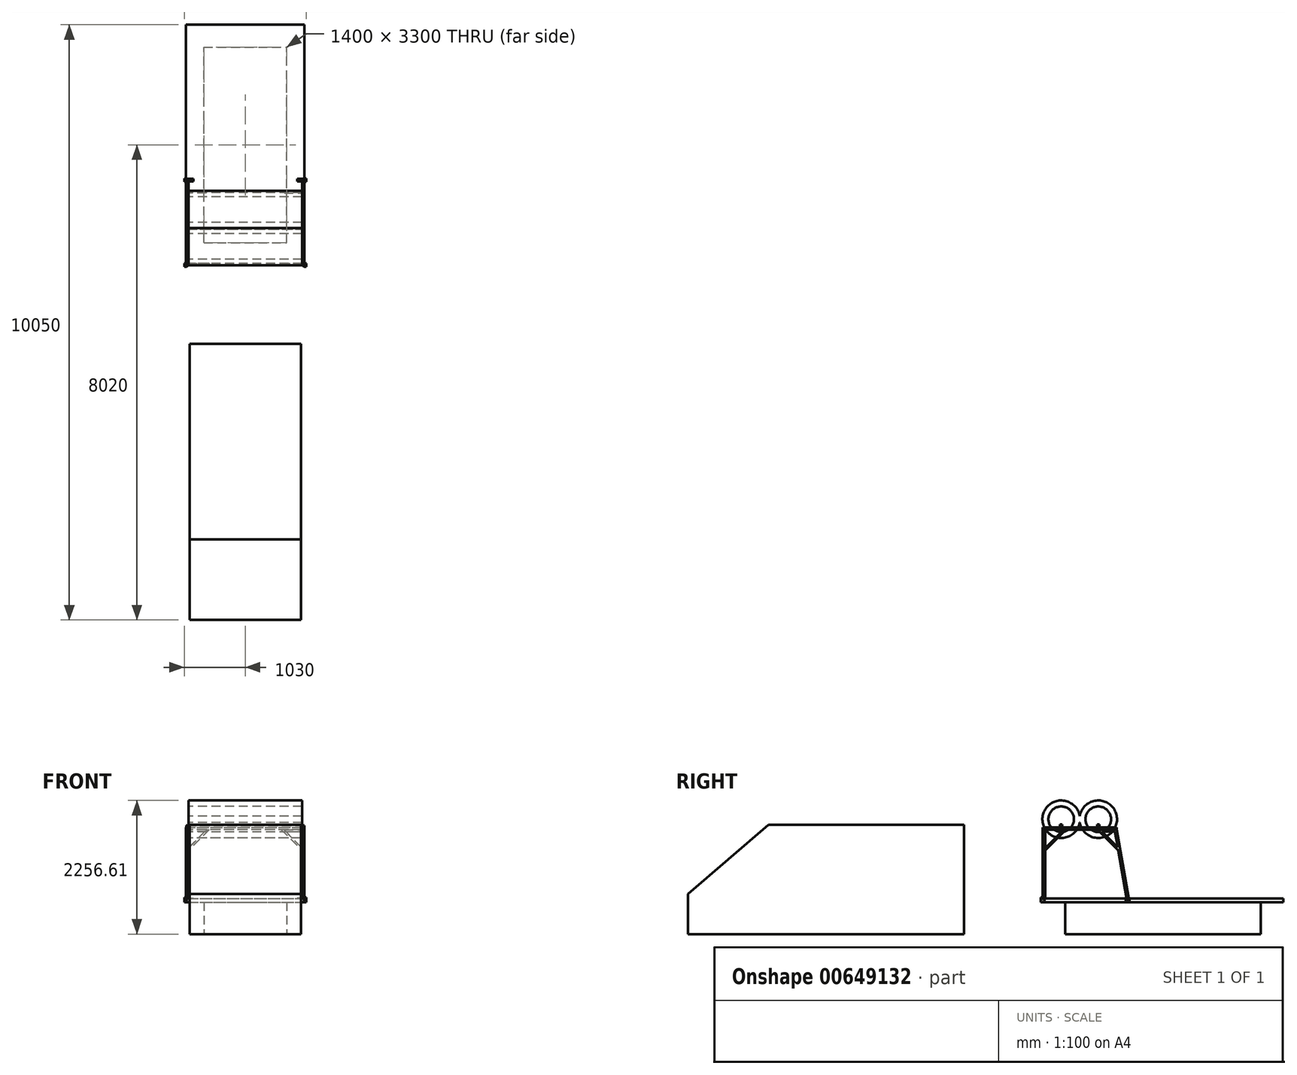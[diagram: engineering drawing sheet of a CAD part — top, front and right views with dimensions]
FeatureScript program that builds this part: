
annotation { "Feature Type Name" : "Feature", "Feature Type Description" : "" }
export const myFeature = defineFeature(function(context is Context, id is Id, definition is map)
    precondition{}
    {
        {
            var Q0;
            Q0=qCreatedBy(makeId("Top.planeOp"),FACE);
            cPlane(context, id + "F0", {"entities" : qUnion([Q0]), "cplaneType" : CPlaneType.OFFSET, "offset" : 600 * mm, "width" : 150 * mm, "height" : 150 * mm});
        }
        {
            var Q0;
            Q0=qCreatedBy(id+"F0.planeOp",FACE);
            var sketch = newSketch(context, id + "F1", { "sketchPlane" : qUnion([Q0])});
            skLineSegment(sketch, "E0.bottom", {"start": v(-1000, 2030) * mm, "end": v(1000, 2030) * mm});
            skLineSegment(sketch, "E0.top", {"start": v(-1000, -2030) * mm, "end": v(1000, -2030) * mm});
            skLineSegment(sketch, "E0.left", {"start": v(-1000, 2030) * mm, "end": v(-1000, -2030) * mm});
            skLineSegment(sketch, "E0.right", {"start": v(1000, 2030) * mm, "end": v(1000, -2030) * mm});
            skSolve(sketch);
        }
        {
            var Q0;
            Q0 = qSketchRegion(id + "F1", true);
            var Q1;
            Q1=qCreatedBy(id+"F0.planeOp",FACE);
            extrude(context, id + "F2", {"entities" : qUnion([Q0]), "oppositeDirection" : true, "depth" : 60 * mm, "endBoundEntityFace" : qUnion([Q1]), "offsetDistance" : 25 * mm});
        }
        {
            var Q0;
            Q0=qCreatedBy(id+"F0.planeOp",FACE);
            var sketch = newSketch(context, id + "F3", { "sketchPlane" : qUnion([Q0])});
            skLineSegment(sketch, "E1.bottom", {"start": v(-1030, -2000) * mm, "end": v(-990, -2000) * mm});
            skLineSegment(sketch, "E1.top", {"start": v(-1030, -2060) * mm, "end": v(-990, -2060) * mm});
            skLineSegment(sketch, "E1.left", {"start": v(-1030, -2000) * mm, "end": v(-1030, -2060) * mm});
            skLineSegment(sketch, "E1.right", {"start": v(-990, -2000) * mm, "end": v(-990, -2060) * mm});
            skLineSegment(sketch, "E2.MirrorCS", {"start": v(1030, -2000) * mm, "end": v(990, -2000) * mm});
            skLineSegment(sketch, "E3.MirrorCS", {"start": v(990, -2000) * mm, "end": v(990, -2060) * mm});
            skLineSegment(sketch, "E4.MirrorCS", {"start": v(1030, -2060) * mm, "end": v(990, -2060) * mm});
            skLineSegment(sketch, "E5.MirrorCS", {"start": v(1030, -2000) * mm, "end": v(1030, -2060) * mm});
            skSolve(sketch);
        }
        {
            var Q0;
            Q0=makeQuery(id+"F3.imprint","IMPRINT",FACE,{"disambiguationData":[TD([[makeQuery(id+"F3.imprint","IMPRINT",EDGE,{"derivedFrom":sQuery(id+"F3.wireOp",EDGE,"E1.bottom")}),-1.0]])]});
            var Q1;
            Q1=makeQuery(id+"F3.imprint","IMPRINT",FACE,{"disambiguationData":[TD([[makeQuery(id+"F3.imprint","IMPRINT",EDGE,{"derivedFrom":sQuery(id+"F3.wireOp",EDGE,"E2.MirrorCS")}),1.0]])]});
            extrude(context, id + "F4", {"entities" : qUnion([Q0, Q1]), "operationType" : NewBodyOperationType.ADD, "oppositeDirection" : true, "depth" : 60 * mm, "offsetDistance" : 25 * mm});
        }
        {
            var Q0;
            Q0=makeQuery(id+"F4.boolean.opBoolean","MERGE",FACE,{"derivedFrom":[makeQuery(id+"F2.opExtrude","CAP_FACE",FACE,{"disambiguationData":[OSD([dummyQuery(id+"F0.planeOp",FACE)])],"isStart":false}),makeQuery(id+"F4.opExtrude","CAP_FACE",FACE,{"disambiguationData":[OSD([sQuery(id+"F3.wireOp",EDGE,"E1.bottom"),sQuery(id+"F3.wireOp",EDGE,"E1.top"),sQuery(id+"F3.wireOp",EDGE,"E1.left"),sQuery(id+"F3.wireOp",EDGE,"E1.right")])],"isStart":true})]});
            var sketch = newSketch(context, id + "F5", { "sketchPlane" : qUnion([Q0])});
            skLineSegment(sketch, "E6.MirrorCS", {"start": v(1090.72, -2001.84) * mm, "end": v(1090.72, -2058.16) * mm});
            skLineSegment(sketch, "E7.MirrorCS", {"start": v(1090.72, -2001.84) * mm, "end": v(1076.64, -2001.84) * mm});
            skLineSegment(sketch, "E8.MirrorCS", {"start": v(1076.64, -2001.84) * mm, "end": v(1076.64, -2058.16) * mm});
            skLineSegment(sketch, "E9.MirrorCS", {"start": v(1090.72, -2058.16) * mm, "end": v(1076.64, -2058.16) * mm});
            skLineSegment(sketch, "E10.bottom", {"start": v(-1026, -2004) * mm, "end": v(-994, -2004) * mm});
            skLineSegment(sketch, "E10.top", {"start": v(-1026, -2056) * mm, "end": v(-994, -2056) * mm});
            skLineSegment(sketch, "E10.left", {"start": v(-1026, -2004) * mm, "end": v(-1026, -2056) * mm});
            skLineSegment(sketch, "E10.right", {"start": v(-994, -2004) * mm, "end": v(-994, -2056) * mm});
            skSolve(sketch);
        }
        {
            var Q0;
            Q0=makeQuery(id+"F5.imprint","IMPRINT",FACE,{"disambiguationData":[TD([[makeQuery(id+"F5.imprint","IMPRINT",EDGE,{"derivedFrom":sQuery(id+"F5.wireOp",EDGE,"E10.bottom")}),-1.0]])]});
            extrude(context, id + "F6", {"entities" : qUnion([Q0]), "operationType" : NewBodyOperationType.REMOVE, "endBound" : BoundingType.THROUGH_ALL, "oppositeDirection" : true, "depth" : 25 * mm, "offsetDistance" : 25 * mm});
        }
        {
            var Q0;
            Q0=qCreatedBy(makeId("Top.planeOp"),FACE);
            var sketch = newSketch(context, id + "F7", { "sketchPlane" : qUnion([Q0])});
            skLineSegment(sketch, "E11.bottom", {"start": v(-700, -1650) * mm, "end": v(700, -1650) * mm});
            skLineSegment(sketch, "E11.top", {"start": v(-700, 1650) * mm, "end": v(700, 1650) * mm});
            skLineSegment(sketch, "E11.left", {"start": v(-700, -1650) * mm, "end": v(-700, 1650) * mm});
            skLineSegment(sketch, "E11.right", {"start": v(700, -1650) * mm, "end": v(700, 1650) * mm});
            skSolve(sketch);
        }
        {
            var Q0;
            Q0=makeQuery(id+"F7.imprint","IMPRINT",FACE,{"disambiguationData":[TD([[makeQuery(id+"F7.imprint","IMPRINT",EDGE,{"derivedFrom":sQuery(id+"F7.wireOp",EDGE,"E11.bottom")}),1.0]])]});
            var Q1;
            Q1=makeQuery(id+"F4.boolean.opBoolean","MERGE",FACE,{"derivedFrom":[makeQuery(id+"F2.opExtrude","CAP_FACE",FACE,{"disambiguationData":[OSD([sQuery(id+"F1.wireOp",EDGE,"E0.bottom"),sQuery(id+"F1.wireOp",EDGE,"E0.top"),sQuery(id+"F1.wireOp",EDGE,"E0.left"),sQuery(id+"F1.wireOp",EDGE,"E0.right")])],"isStart":false}),makeQuery(id+"F4.opExtrude","CAP_FACE",FACE,{"disambiguationData":[OSD([sQuery(id+"F3.wireOp",EDGE,"E1.bottom"),sQuery(id+"F3.wireOp",EDGE,"E1.top"),sQuery(id+"F3.wireOp",EDGE,"E1.left"),sQuery(id+"F3.wireOp",EDGE,"E1.right")])],"isStart":false})]});
            extrude(context, id + "F8", {"entities" : qUnion([Q0]), "operationType" : NewBodyOperationType.ADD, "endBound" : BoundingType.UP_TO_SURFACE, "depth" : 25 * mm, "endBoundEntityFace" : qUnion([Q1]), "offsetDistance" : 25 * mm});
        }
        {
            var Q0;
            Q0=makeQuery(id+"F2.opExtrude","SWEPT_FACE",FACE,{"disambiguationData":[OSD([sQuery(id+"F1.wireOp",EDGE,"E0.top")])]});
            cPlane(context, id + "F9", {"entities" : qUnion([Q0]), "cplaneType" : CPlaneType.OFFSET, "offset" : 1415 * mm, "oppositeDirection" : true, "width" : 150 * mm, "height" : 150 * mm});
        }
        {
            var Q0;
            Q0=qCreatedBy(id+"F9.planeOp",FACE);
            var sketch = newSketch(context, id + "F10", { "sketchPlane" : qUnion([Q0])});
            skArc(sketch, "E12", {"start": v(-1017, 580) * mm, "mid": v(-1027, 570) * mm, "end": v(-1017, 560) * mm});
            skLineSegment(sketch, "E13", {"start": v(-1017, 580) * mm, "end": v(-1000, 580) * mm});
            skLineSegment(sketch, "E14", {"start": v(-1000, 580) * mm, "end": v(-1000, 560) * mm});
            skLineSegment(sketch, "E15", {"start": v(-1000, 560) * mm, "end": v(-1017, 560) * mm});
            skCircle(sketch, "E16", {"center": v(-1017, 570) * mm, "radius": 6 * mm});
            skSolve(sketch);
        }
        {
            var Q0;
            Q0=makeQuery(id+"F10.imprint","IMPRINT",FACE,{"disambiguationData":[TD([[makeQuery(id+"F10.imprint","IMPRINT",EDGE,{"derivedFrom":sQuery(id+"F10.wireOp",EDGE,"E12")}),1.0]])]});
            extrude(context, id + "F11", {"entities" : qUnion([Q0]), "oppositeDirection" : true, "depth" : 40 * mm, "offsetDistance" : 25 * mm});
        }
        {
            var Q0;
            Q0=makeQuery(id+"F11.opExtrude","SWEPT_BODY",BODY,{"disambiguationData":[OSD([sQuery(id+"F10.wireOp",EDGE,"E12"),sQuery(id+"F10.wireOp",EDGE,"E13"),sQuery(id+"F10.wireOp",EDGE,"E14"),sQuery(id+"F10.wireOp",EDGE,"E15"),sQuery(id+"F10.wireOp",EDGE,"E16")])]});
            var Q1;
            Q1=qCreatedBy(makeId("Right.planeOp"),FACE);
            mirror(context, id + "F12", {"operationType" : NewBodyOperationType.ADD, "entities" : qUnion([Q0]), "mirrorPlane" : qUnion([Q1])});
        }
        {
            var Q0;
            Q0=qCreatedBy(id+"F0.planeOp",FACE);
            cPlane(context, id + "F13", {"entities" : qUnion([Q0]), "cplaneType" : CPlaneType.OFFSET, "offset" : 1200 * mm, "width" : 150 * mm, "height" : 150 * mm});
        }
        {
            var Q0;
            Q0=makeQuery(id+"F4.boolean.opBoolean","MERGE",FACE,{"derivedFrom":[makeQuery(id+"F2.opExtrude","CAP_FACE",FACE,{"disambiguationData":[OSD([sQuery(id+"F1.wireOp",EDGE,"E0.bottom"),sQuery(id+"F1.wireOp",EDGE,"E0.top"),sQuery(id+"F1.wireOp",EDGE,"E0.left"),sQuery(id+"F1.wireOp",EDGE,"E0.right")])],"isStart":true}),makeQuery(id+"F4.opExtrude","CAP_FACE",FACE,{"disambiguationData":[OSD([sQuery(id+"F3.wireOp",EDGE,"E1.bottom"),sQuery(id+"F3.wireOp",EDGE,"E1.top"),sQuery(id+"F3.wireOp",EDGE,"E1.left"),sQuery(id+"F3.wireOp",EDGE,"E1.right")])],"isStart":true}),makeQuery(id+"F4.opExtrude","CAP_FACE",FACE,{"disambiguationData":[OSD([sQuery(id+"F3.wireOp",EDGE,"E2.MirrorCS"),sQuery(id+"F3.wireOp",EDGE,"E3.MirrorCS"),sQuery(id+"F3.wireOp",EDGE,"E4.MirrorCS"),sQuery(id+"F3.wireOp",EDGE,"E5.MirrorCS")])],"isStart":true})]});
            var sketch = newSketch(context, id + "F14", { "sketchPlane" : qUnion([Q0])});
            skLineSegment(sketch, "E17.bottom", {"start": v(-1027, -575) * mm, "end": v(-877, -575) * mm});
            skLineSegment(sketch, "E17.top", {"start": v(-1027, -615) * mm, "end": v(-877, -615) * mm});
            skLineSegment(sketch, "E17.left", {"start": v(-1027, -575) * mm, "end": v(-1027, -615) * mm});
            skLineSegment(sketch, "E17.right", {"start": v(-877, -575) * mm, "end": v(-877, -615) * mm});
            skSolve(sketch);
        }
        {
            var Q0;
            Q0 = qSketchRegion(id + "F14", true);
            extrude(context, id + "F15", {"entities" : qUnion([Q0]), "depth" : 10 * mm, "offsetDistance" : 25 * mm});
        }
        {
            var Q0;
            Q0=makeQuery(id+"F15.opExtrude","SWEPT_FACE",FACE,{"disambiguationData":[OSD([sQuery(id+"F14.wireOp",EDGE,"E17.top")])]});
            var sketch = newSketch(context, id + "F16", { "sketchPlane" : qUnion([Q0])});
            skLineSegment(sketch, "E18", {"start": v(-1027, 610) * mm, "end": v(-1027, 570) * mm});
            skLineSegment(sketch, "E19", {"start": v(-1017, 560) * mm, "end": v(-1017, 560) * mm});
            skLineSegment(sketch, "E20", {"start": v(-1007, 570) * mm, "end": v(-1007, 610) * mm});
            skLineSegment(sketch, "E21", {"start": v(-1007, 610) * mm, "end": v(-1027, 610) * mm});
            skPoint(sketch, "E22.visualSharp", {"position": v(-1027, 560) * mm});
            skArc(sketch, "E22.filletArc", {"start": v(-1027, 570) * mm, "mid": v(-1024.07, 562.93) * mm, "end": v(-1017, 560) * mm});
            skCircle(sketch, "E23", {"center": v(-1017, 570) * mm, "radius": 6 * mm});
            skPoint(sketch, "E24.visualSharp", {"position": v(-1007, 560) * mm});
            skArc(sketch, "E24.filletArc", {"start": v(-1017, 560) * mm, "mid": v(-1009.93, 562.93) * mm, "end": v(-1007, 570) * mm});
            skSolve(sketch);
        }
        {
            var Q0;
            Q0 = qSketchRegion(id + "F16", true);
            extrude(context, id + "F17", {"entities" : qUnion([Q0]), "depth" : 10 * mm, "offsetDistance" : 25 * mm});
        }
        {
            var Q0;
            Q0=makeQuery(id+"F17.opExtrude","SWEPT_BODY",BODY,{"disambiguationData":[OSD([sQuery(id+"F16.wireOp",EDGE,"E18"),sQuery(id+"F16.wireOp",EDGE,"E20"),sQuery(id+"F16.wireOp",EDGE,"E21"),sQuery(id+"F16.wireOp",EDGE,"E22.filletArc"),sQuery(id+"F16.wireOp",EDGE,"E23"),sQuery(id+"F16.wireOp",EDGE,"E24.filletArc")])]});
            transform(context, id + "F18", {"entities" : qUnion([Q0]), "transformType" : TransformType.TRANSLATION_3D, "dx" : 0 * mm, "dy" : 50 * mm, "dz" : 0 * mm, "makeCopy" : true});
        }
        {
            var Q0;
            Q0=makeQuery(id+"F4.boolean.opBoolean","MERGE",FACE,{"derivedFrom":[makeQuery(id+"F2.opExtrude","CAP_FACE",FACE,{"disambiguationData":[OSD([sQuery(id+"F1.wireOp",EDGE,"E0.bottom"),sQuery(id+"F1.wireOp",EDGE,"E0.top"),sQuery(id+"F1.wireOp",EDGE,"E0.left"),sQuery(id+"F1.wireOp",EDGE,"E0.right")])],"isStart":true}),makeQuery(id+"F4.opExtrude","CAP_FACE",FACE,{"disambiguationData":[OSD([sQuery(id+"F3.wireOp",EDGE,"E1.bottom"),sQuery(id+"F3.wireOp",EDGE,"E1.top"),sQuery(id+"F3.wireOp",EDGE,"E1.left"),sQuery(id+"F3.wireOp",EDGE,"E1.right")])],"isStart":true}),makeQuery(id+"F4.opExtrude","CAP_FACE",FACE,{"disambiguationData":[OSD([sQuery(id+"F3.wireOp",EDGE,"E2.MirrorCS"),sQuery(id+"F3.wireOp",EDGE,"E3.MirrorCS"),sQuery(id+"F3.wireOp",EDGE,"E4.MirrorCS"),sQuery(id+"F3.wireOp",EDGE,"E5.MirrorCS")])],"isStart":true})]});
            var sketch = newSketch(context, id + "F19", { "sketchPlane" : qUnion([Q0])});
            skLineSegment(sketch, "E25.bottom", {"start": v(-1000, -1990) * mm, "end": v(-960, -1990) * mm});
            skLineSegment(sketch, "E25.right", {"start": v(-960, -1990) * mm, "end": v(-960, -2030) * mm});
            skLineSegment(sketch, "E26", {"start": v(-1030, -2060) * mm, "end": v(-1030, -2000) * mm});
            skLineSegment(sketch, "E27", {"start": v(-1030, -2000) * mm, "end": v(-1000, -1990) * mm});
            skLineSegment(sketch, "E28", {"start": v(-960, -2030) * mm, "end": v(-990, -2060) * mm});
            skLineSegment(sketch, "E29", {"start": v(-990, -2060) * mm, "end": v(-1030, -2060) * mm});
            skSolve(sketch);
        }
        {
            var Q0;
            Q0 = qSketchRegion(id + "F19", true);
            extrude(context, id + "F20", {"entities" : qUnion([Q0]), "depth" : 20 * mm, "offsetDistance" : 25 * mm});
        }
        {
            var Q0;
            Q0=makeQuery(id+"F20.opExtrude","CAP_FACE",FACE,{"disambiguationData":[OSD([sQuery(id+"F19.wireOp",EDGE,"E25.bottom"),sQuery(id+"F19.wireOp",EDGE,"E25.right"),sQuery(id+"F19.wireOp",EDGE,"E26"),sQuery(id+"F19.wireOp",EDGE,"E27"),sQuery(id+"F19.wireOp",EDGE,"E28"),sQuery(id+"F19.wireOp",EDGE,"E29")])],"isStart":false});
            var sketch = newSketch(context, id + "F21", { "sketchPlane" : qUnion([Q0])});
            skLineSegment(sketch, "E30.bottom", {"start": v(-1000, -1990) * mm, "end": v(-960, -1990) * mm});
            skLineSegment(sketch, "E30.top", {"start": v(-1000, -2030) * mm, "end": v(-960, -2030) * mm});
            skLineSegment(sketch, "E30.left", {"start": v(-1000, -1990) * mm, "end": v(-1000, -2030) * mm});
            skLineSegment(sketch, "E30.right", {"start": v(-960, -1990) * mm, "end": v(-960, -2030) * mm});
            skSolve(sketch);
        }
        {
            var Q0;
            Q0 = qSketchRegion(id + "F21", true);
            var Q1;
            Q1=qCreatedBy(id+"F13.planeOp",FACE);
            extrude(context, id + "F22", {"entities" : qUnion([Q0]), "endBound" : BoundingType.UP_TO_SURFACE, "depth" : 518 * mm, "endBoundEntityFace" : qUnion([Q1]), "offsetDistance" : 25 * mm});
        }
        {
            var Q0;
            Q0=makeQuery(id+"F22.opExtrude","SWEPT_FACE",FACE,{"disambiguationData":[OSD([sQuery(id+"F21.wireOp",EDGE,"E30.bottom")])]});
            var sketch = newSketch(context, id + "F23", { "sketchPlane" : qUnion([Q0])});
            skLineSegment(sketch, "E31.bottom", {"start": v(960, 1800) * mm, "end": v(995, 1800) * mm});
            skLineSegment(sketch, "E31.top", {"start": v(960, 1765) * mm, "end": v(995, 1765) * mm});
            skLineSegment(sketch, "E31.left", {"start": v(960, 1800) * mm, "end": v(960, 1765) * mm});
            skLineSegment(sketch, "E31.right", {"start": v(995, 1800) * mm, "end": v(995, 1765) * mm});
            skSolve(sketch);
        }
        {
            var Q0;
            Q0 = qSketchRegion(id + "F23", true);
            extrude(context, id + "F24", {"entities" : qUnion([Q0]), "depth" : 1210 * mm, "offsetDistance" : 25 * mm});
        }
        {
            var Q0;
            Q0=makeQuery(id+"F22.opExtrude","SWEPT_BODY",BODY,{"disambiguationData":[OSD([sQuery(id+"F21.wireOp",EDGE,"E30.bottom"),sQuery(id+"F21.wireOp",EDGE,"E30.top"),sQuery(id+"F21.wireOp",EDGE,"E30.left"),sQuery(id+"F21.wireOp",EDGE,"E30.right")])]});
            var Q1;
            Q1=makeQuery(id+"F24.opExtrude","SWEPT_BODY",BODY,{"disambiguationData":[OSD([sQuery(id+"F23.wireOp",EDGE,"E31.bottom"),sQuery(id+"F23.wireOp",EDGE,"E31.top"),sQuery(id+"F23.wireOp",EDGE,"E31.left"),sQuery(id+"F23.wireOp",EDGE,"E31.right")])]});
            var Q2;
            Q2=makeQuery(id+"F20.opExtrude","SWEPT_BODY",BODY,{"disambiguationData":[OSD([sQuery(id+"F19.wireOp",EDGE,"E25.bottom"),sQuery(id+"F19.wireOp",EDGE,"E25.right"),sQuery(id+"F19.wireOp",EDGE,"E26"),sQuery(id+"F19.wireOp",EDGE,"E27"),sQuery(id+"F19.wireOp",EDGE,"E28"),sQuery(id+"F19.wireOp",EDGE,"E29")])]});
            var Q3;
            Q3=makeQuery(id+"F18.opPattern","COPY",BODY,{"derivedFrom":makeQuery(id+"F17.opExtrude","SWEPT_BODY",BODY,{"disambiguationData":[OSD([sQuery(id+"F16.wireOp",EDGE,"E18"),sQuery(id+"F16.wireOp",EDGE,"E20"),sQuery(id+"F16.wireOp",EDGE,"E21"),sQuery(id+"F16.wireOp",EDGE,"E22.filletArc"),sQuery(id+"F16.wireOp",EDGE,"E23"),sQuery(id+"F16.wireOp",EDGE,"E24.filletArc")])]}),"instanceName":"1"});
            var Q4;
            Q4=makeQuery(id+"F17.opExtrude","SWEPT_BODY",BODY,{"disambiguationData":[OSD([sQuery(id+"F16.wireOp",EDGE,"E18"),sQuery(id+"F16.wireOp",EDGE,"E20"),sQuery(id+"F16.wireOp",EDGE,"E21"),sQuery(id+"F16.wireOp",EDGE,"E22.filletArc"),sQuery(id+"F16.wireOp",EDGE,"E23"),sQuery(id+"F16.wireOp",EDGE,"E24.filletArc")])]});
            var Q5;
            Q5=makeQuery(id+"F15.opExtrude","SWEPT_BODY",BODY,{"disambiguationData":[OSD([sQuery(id+"F14.wireOp",EDGE,"E17.bottom"),sQuery(id+"F14.wireOp",EDGE,"E17.top"),sQuery(id+"F14.wireOp",EDGE,"E17.left"),sQuery(id+"F14.wireOp",EDGE,"E17.right")])]});
            var Q6;
            Q6=makeQuery(id+"F2.opExtrude","SWEPT_BODY",BODY,{"disambiguationData":[OSD([sQuery(id+"F1.wireOp",EDGE,"E0.bottom"),sQuery(id+"F1.wireOp",EDGE,"E0.top"),sQuery(id+"F1.wireOp",EDGE,"E0.left"),sQuery(id+"F1.wireOp",EDGE,"E0.right")])]});
            var Q7;
            Q7=qCreatedBy(makeId("Right.planeOp"),FACE);
            mirror(context, id + "F25", {"entities" : qUnion([Q0, Q1, Q2, Q3, Q4, Q5, Q6]), "mirrorPlane" : qUnion([Q7])});
        }
        {
            var Q0;
            Q0=qCreatedBy(makeId("Right.planeOp"),FACE);
            var sketch = newSketch(context, id + "F26", { "sketchPlane" : qUnion([Q0])});
            skLineSegment(sketch, "E32.bottom", {"start": v(-780, 1765) * mm, "end": v(-810, 1765) * mm});
            skLineSegment(sketch, "E32.top", {"start": v(-780, 1795) * mm, "end": v(-810, 1795) * mm});
            skLineSegment(sketch, "E32.left", {"start": v(-780, 1765) * mm, "end": v(-780, 1795) * mm});
            skLineSegment(sketch, "E32.right", {"start": v(-810, 1765) * mm, "end": v(-810, 1795) * mm});
            skLineSegment(sketch, "E33.bottom", {"start": v(-1390, 1800) * mm, "end": v(-1420, 1800) * mm});
            skLineSegment(sketch, "E33.top", {"start": v(-1390, 1830) * mm, "end": v(-1420, 1830) * mm});
            skLineSegment(sketch, "E33.left", {"start": v(-1390, 1800) * mm, "end": v(-1390, 1830) * mm});
            skLineSegment(sketch, "E33.right", {"start": v(-1420, 1800) * mm, "end": v(-1420, 1830) * mm});
            skLineSegment(sketch, "E34.bottom", {"start": v(-2000, 1795) * mm, "end": v(-2030, 1795) * mm});
            skLineSegment(sketch, "E34.top", {"start": v(-2000, 1765) * mm, "end": v(-2030, 1765) * mm});
            skLineSegment(sketch, "E34.left", {"start": v(-2000, 1795) * mm, "end": v(-2000, 1765) * mm});
            skLineSegment(sketch, "E34.right", {"start": v(-2030, 1795) * mm, "end": v(-2030, 1765) * mm});
            skSolve(sketch);
        }
        {
            var Q0;
            Q0=makeQuery(id+"F26.imprint","IMPRINT",FACE,{"disambiguationData":[TD([[makeQuery(id+"F26.imprint","IMPRINT",EDGE,{"derivedFrom":sQuery(id+"F26.wireOp",EDGE,"E32.bottom")}),-1.0]])]});
            var Q1;
            Q1=makeQuery(id+"F26.imprint","IMPRINT",FACE,{"disambiguationData":[TD([[makeQuery(id+"F26.imprint","IMPRINT",EDGE,{"derivedFrom":sQuery(id+"F26.wireOp",EDGE,"E34.bottom")}),1.0]])]});
            extrude(context, id + "F27", {"entities" : qUnion([Q0, Q1]), "endBound" : BoundingType.UP_TO_NEXT, "depth" : 25 * mm, "offsetDistance" : 25 * mm, "hasSecondDirection" : true, "secondDirectionBound" : SecondDirectionBoundingType.UP_TO_NEXT, "secondDirectionOppositeDirection" : true, "secondDirectionDepth" : 25 * mm});
        }
        {
            var Q0;
            Q0=makeQuery(id+"F26.imprint","IMPRINT",FACE,{"disambiguationData":[TD([[makeQuery(id+"F26.imprint","IMPRINT",EDGE,{"derivedFrom":sQuery(id+"F26.wireOp",EDGE,"E33.bottom")}),-1.0]])]});
            var Q1;
            Q1=makeQuery(id+"F24.opExtrude","SWEPT_FACE",FACE,{"disambiguationData":[OSD([sQuery(id+"F23.wireOp",EDGE,"E31.right")])]});
            var Q2;
            Q2=makeQuery(id+"F25.opPattern","COPY",FACE,{"derivedFrom":makeQuery(id+"F24.opExtrude","SWEPT_FACE",FACE,{"disambiguationData":[OSD([sQuery(id+"F23.wireOp",EDGE,"E31.right")])]}),"instanceName":"1"});
            extrude(context, id + "F28", {"entities" : qUnion([Q0]), "endBound" : BoundingType.UP_TO_SURFACE, "oppositeDirection" : true, "depth" : 25 * mm, "endBoundEntityFace" : qUnion([Q1]), "offsetDistance" : 25 * mm, "hasSecondDirection" : true, "secondDirectionBound" : SecondDirectionBoundingType.UP_TO_SURFACE, "secondDirectionOppositeDirection" : false, "secondDirectionDepth" : 25 * mm, "secondDirectionBoundEntityFace" : qUnion([Q2])});
        }
        {
            var Q0;
            Q0=makeQuery(id+"F24.opExtrude","SWEPT_FACE",FACE,{"disambiguationData":[OSD([sQuery(id+"F23.wireOp",EDGE,"E31.right")])]});
            var sketch = newSketch(context, id + "F29", { "sketchPlane" : qUnion([Q0])});
            skLineSegment(sketch, "E35", {"start": v(577.47, 610) * mm, "end": v(780, 1765) * mm});
            skLineSegment(sketch, "E36", {"start": v(780, 1765) * mm, "end": v(1107.1, 1765) * mm});
            skLineSegment(sketch, "E37", {"start": v(1107.1, 1765) * mm, "end": v(1072.1, 1730) * mm});
            skLineSegment(sketch, "E38", {"start": v(1029.66, 1730) * mm, "end": v(809.4, 1730) * mm});
            skLineSegment(sketch, "E39", {"start": v(809.4, 1730) * mm, "end": v(762.56, 1462.9) * mm});
            skLineSegment(sketch, "E40", {"start": v(613, 610) * mm, "end": v(577.47, 610) * mm});
            skLineSegment(sketch, "E41", {"start": v(1072.1, 1730) * mm, "end": v(753.54, 1411.45) * mm});
            skLineSegment(sketch, "E42", {"start": v(762.56, 1462.9) * mm, "end": v(1029.66, 1730) * mm});
            skLineSegment(sketch, "E43.trimOffspring", {"start": v(753.54, 1411.45) * mm, "end": v(613, 610) * mm});
            skSolve(sketch);
        }
        {
            var Q0;
            Q0 = qSketchRegion(id + "F29", true);
            extrude(context, id + "F30", {"entities" : qUnion([Q0]), "oppositeDirection" : true, "depth" : 35 * mm, "offsetDistance" : 25 * mm});
        }
        {
            var Q0;
            Q0=makeQuery(id+"F24.opExtrude","SWEPT_FACE",FACE,{"disambiguationData":[OSD([sQuery(id+"F23.wireOp",EDGE,"E31.left")])]});
            var sketch = newSketch(context, id + "F31", { "sketchPlane" : qUnion([Q0])});
            skLineSegment(sketch, "E44.bottom", {"start": v(-780, 1765) * mm, "end": v(-815, 1765) * mm});
            skLineSegment(sketch, "E44.top", {"start": v(-780, 1730) * mm, "end": v(-815, 1730) * mm});
            skLineSegment(sketch, "E44.left", {"start": v(-780, 1765) * mm, "end": v(-780, 1730) * mm});
            skLineSegment(sketch, "E44.right", {"start": v(-815, 1765) * mm, "end": v(-815, 1730) * mm});
            skLineSegment(sketch, "E45.bottom", {"start": v(-812.5, 1762.5) * mm, "end": v(-782.5, 1762.5) * mm});
            skLineSegment(sketch, "E45.top", {"start": v(-812.5, 1732.5) * mm, "end": v(-782.5, 1732.5) * mm});
            skLineSegment(sketch, "E45.left", {"start": v(-812.5, 1762.5) * mm, "end": v(-812.5, 1732.5) * mm});
            skLineSegment(sketch, "E45.right", {"start": v(-782.5, 1762.5) * mm, "end": v(-782.5, 1732.5) * mm});
            skSolve(sketch);
        }
        {
            var Q0;
            Q0 = qSketchRegion(id + "F31", true);
            extrude(context, id + "F32", {"entities" : qUnion([Q0]), "depth" : 300 * mm, "offsetDistance" : 25 * mm});
        }
        {
            var Q0;
            Q0=makeQuery(id+"F30.opExtrude","SWEPT_BODY",BODY,{"disambiguationData":[OSD([sQuery(id+"F29.wireOp",EDGE,"E35"),sQuery(id+"F29.wireOp",EDGE,"E36"),sQuery(id+"F29.wireOp",EDGE,"E37"),sQuery(id+"F29.wireOp",EDGE,"E38"),sQuery(id+"F29.wireOp",EDGE,"E39"),sQuery(id+"F29.wireOp",EDGE,"E40")])]});
            var Q1;
            Q1=makeQuery(id+"F32.opExtrude","SWEPT_BODY",BODY,{"disambiguationData":[OSD([sQuery(id+"F31.wireOp",EDGE,"E44.bottom"),sQuery(id+"F31.wireOp",EDGE,"E44.top"),sQuery(id+"F31.wireOp",EDGE,"E44.left"),sQuery(id+"F31.wireOp",EDGE,"E44.right"),sQuery(id+"F31.wireOp",EDGE,"E45.bottom"),sQuery(id+"F31.wireOp",EDGE,"E45.top"),sQuery(id+"F31.wireOp",EDGE,"E45.left"),sQuery(id+"F31.wireOp",EDGE,"E45.right")])]});
            var Q2;
            Q2=qCreatedBy(makeId("Right.planeOp"),FACE);
            mirror(context, id + "F33", {"entities" : qUnion([Q0, Q1]), "mirrorPlane" : qUnion([Q2])});
        }
        {
            var Q0;
            Q0=qCreatedBy(makeId("Right.planeOp"),FACE);
            var sketch = newSketch(context, id + "F34", { "sketchPlane" : qUnion([Q0])});
            skCircle(sketch, "E46", {"center": v(-1092.34, 1939.46) * mm, "radius": 317.15 * mm});
            skCircle(sketch, "E47", {"center": v(-1717.66, 1939.46) * mm, "radius": 317.15 * mm});
            skCircle(sketch, "E48", {"center": v(-1092.34, 1939.46) * mm, "radius": 216 * mm});
            skCircle(sketch, "E49", {"center": v(-1717.66, 1939.46) * mm, "radius": 216 * mm});
            skSolve(sketch);
        }
        {
            var Q0;
            Q0 = qSketchRegion(id + "F34", true);
            var Q1;
            Q1=makeQuery(id+"F25.opPattern","COPY",FACE,{"derivedFrom":makeQuery(id+"F24.opExtrude","SWEPT_FACE",FACE,{"disambiguationData":[OSD([sQuery(id+"F23.wireOp",EDGE,"E31.left")])]}),"instanceName":"1"});
            var Q2;
            Q2=makeQuery(id+"F24.opExtrude","SWEPT_FACE",FACE,{"disambiguationData":[OSD([sQuery(id+"F23.wireOp",EDGE,"E31.left")])]});
            extrude(context, id + "F35", {"entities" : qUnion([Q0]), "endBound" : BoundingType.UP_TO_SURFACE, "depth" : 25 * mm, "endBoundEntityFace" : qUnion([Q1]), "offsetDistance" : 25 * mm, "hasSecondDirection" : true, "secondDirectionBound" : SecondDirectionBoundingType.UP_TO_SURFACE, "secondDirectionOppositeDirection" : true, "secondDirectionDepth" : 25 * mm, "secondDirectionBoundEntityFace" : qUnion([Q2])});
        }
        {
            var Q0;
            Q0=makeQuery(id+"F22.opExtrude","SWEPT_FACE",FACE,{"disambiguationData":[OSD([sQuery(id+"F21.wireOp",EDGE,"E30.top")])]});
            var sketch = newSketch(context, id + "F36", { "sketchPlane" : qUnion([Q0])});
            skLineSegment(sketch, "E50", {"start": v(-960, 1453.87) * mm, "end": v(-648.87, 1765) * mm});
            skLineSegment(sketch, "E51", {"start": v(-648.87, 1765) * mm, "end": v(-606.45, 1765) * mm});
            skLineSegment(sketch, "E52", {"start": v(-606.45, 1765) * mm, "end": v(-960, 1411.45) * mm});
            skLineSegment(sketch, "E53", {"start": v(-960, 1411.45) * mm, "end": v(-960, 1453.87) * mm});
            skSolve(sketch);
        }
        {
            var Q0;
            Q0 = qSketchRegion(id + "F36", true);
            extrude(context, id + "F37", {"entities" : qUnion([Q0]), "oppositeDirection" : true, "depth" : 30 * mm, "offsetDistance" : 25 * mm});
        }
        {
            var Q0;
            Q0=makeQuery(id+"F37.opExtrude","SWEPT_BODY",BODY,{"disambiguationData":[OSD([sQuery(id+"F36.wireOp",EDGE,"E50"),sQuery(id+"F36.wireOp",EDGE,"E51"),sQuery(id+"F36.wireOp",EDGE,"E52"),sQuery(id+"F36.wireOp",EDGE,"E53")])]});
            var Q1;
            Q1=qCreatedBy(makeId("Right.planeOp"),FACE);
            mirror(context, id + "F38", {"entities" : qUnion([Q0]), "mirrorPlane" : qUnion([Q1])});
        }
        {
            var Q0;
            Q0=makeQuery(id+"F24.opExtrude","SWEPT_FACE",FACE,{"disambiguationData":[OSD([sQuery(id+"F23.wireOp",EDGE,"E31.right")])]});
            var sketch = newSketch(context, id + "F39", { "sketchPlane" : qUnion([Q0])});
            skLineSegment(sketch, "E54", {"start": v(1678.87, 1765) * mm, "end": v(1990, 1453.87) * mm});
            skLineSegment(sketch, "E55", {"start": v(1990, 1453.87) * mm, "end": v(1990, 1411.45) * mm});
            skLineSegment(sketch, "E56", {"start": v(1990, 1411.45) * mm, "end": v(1636.45, 1765) * mm});
            skLineSegment(sketch, "E57", {"start": v(1636.45, 1765) * mm, "end": v(1678.87, 1765) * mm});
            skSolve(sketch);
        }
        {
            var Q0;
            Q0 = qSketchRegion(id + "F39", true);
            extrude(context, id + "F40", {"entities" : qUnion([Q0]), "oppositeDirection" : true, "depth" : 30 * mm, "offsetDistance" : 25 * mm});
        }
        {
            var Q0;
            Q0=makeQuery(id+"F40.opExtrude","SWEPT_BODY",BODY,{"disambiguationData":[OSD([sQuery(id+"F39.wireOp",EDGE,"E54"),sQuery(id+"F39.wireOp",EDGE,"E55"),sQuery(id+"F39.wireOp",EDGE,"E56"),sQuery(id+"F39.wireOp",EDGE,"E57")])]});
            var Q1;
            Q1=qCreatedBy(makeId("Right.planeOp"),FACE);
            mirror(context, id + "F41", {"entities" : qUnion([Q0]), "mirrorPlane" : qUnion([Q1])});
        }
        {
            var Q0;
            Q0=makeQuery(id+"F24.opExtrude","SWEPT_FACE",FACE,{"disambiguationData":[OSD([sQuery(id+"F23.wireOp",EDGE,"E31.bottom")])]});
            var sketch = newSketch(context, id + "F42", { "sketchPlane" : qUnion([Q0])});
            skLineSegment(sketch, "E58", {"start": v(-990, -1738) * mm, "end": v(-960, -1738) * mm});
            skLineSegment(sketch, "E59", {"start": v(-960, -1738) * mm, "end": v(-960, -1698) * mm});
            skLineSegment(sketch, "E60", {"start": v(-960, -1698) * mm, "end": v(-990, -1698) * mm});
            skLineSegment(sketch, "E61", {"start": v(-990, -1698) * mm, "end": v(-990, -1701) * mm});
            skLineSegment(sketch, "E62", {"start": v(-990, -1701) * mm, "end": v(-963, -1701) * mm});
            skLineSegment(sketch, "E63", {"start": v(-963, -1701) * mm, "end": v(-963, -1735) * mm});
            skLineSegment(sketch, "E64", {"start": v(-963, -1735) * mm, "end": v(-990, -1735) * mm});
            skLineSegment(sketch, "E65", {"start": v(-990, -1735) * mm, "end": v(-990, -1738) * mm});
            skSolve(sketch);
        }
        {
            var Q0;
            Q0 = qSketchRegion(id + "F42", true);
            extrude(context, id + "F43", {"entities" : qUnion([Q0]), "depth" : 50 * mm, "offsetDistance" : 25 * mm});
        }
        {
            var Q0;
            Q0=makeQuery(id+"F43.opExtrude","CAP_EDGE",EDGE,{"disambiguationData":[OSD([sQuery(id+"F42.wireOp",EDGE,"E65")])],"isStart":false});
            var Q1;
            Q1=makeQuery(id+"F43.opExtrude","CAP_EDGE",EDGE,{"disambiguationData":[OSD([sQuery(id+"F42.wireOp",EDGE,"E61")])],"isStart":false});
            chamfer(context, id + "F44", {"entities" : qUnion([Q0, Q1]), "chamferType" : ChamferType.TWO_OFFSETS, "width1" : 15 * mm, "oppositeDirection" : false, "width2" : 45 * mm, "tangentPropagation" : true});
        }
        {
            var Q0;
            Q0=makeQuery(id+"F43.opExtrude","SWEPT_FACE",FACE,{"disambiguationData":[OSD([sQuery(id+"F42.wireOp",EDGE,"E63")])]});
            var sketch = newSketch(context, id + "F45", { "sketchPlane" : qUnion([Q0])});
            skCircle(sketch, "E66", {"center": v(1718, 1830) * mm, "radius": 10 * mm});
            skSolve(sketch);
        }
        {
            var Q0;
            Q0=sQuery(id+"F45.wireOp",VERTEX,"E66.center");
            var Q1;
            Q1=makeQuery(id+"F43.opExtrude","SWEPT_BODY",BODY,{"disambiguationData":[OSD([sQuery(id+"F42.wireOp",EDGE,"E58"),sQuery(id+"F42.wireOp",EDGE,"E59"),sQuery(id+"F42.wireOp",EDGE,"E60"),sQuery(id+"F42.wireOp",EDGE,"E61"),sQuery(id+"F42.wireOp",EDGE,"E62"),sQuery(id+"F42.wireOp",EDGE,"E63"),sQuery(id+"F42.wireOp",EDGE,"E64"),sQuery(id+"F42.wireOp",EDGE,"E65")])]});
            hole(context, id + "F46", {"style" : HoleStyle.SIMPLE, "endStyle" : HoleEndStyle.THROUGH, "holeDiameter" : 20 * mm, "majorDiameter" : 5 * mm, "isTappedThrough" : true, "tappedDepth" : 12 * mm, "tapClearance" : 3, "locations" : qUnion([Q0]), "scope" : qUnion([Q1])});
        }
        {
            var Q0;
            Q0=makeQuery(id+"F43.opExtrude","SWEPT_BODY",BODY,{"disambiguationData":[OSD([sQuery(id+"F42.wireOp",EDGE,"E58"),sQuery(id+"F42.wireOp",EDGE,"E59"),sQuery(id+"F42.wireOp",EDGE,"E60"),sQuery(id+"F42.wireOp",EDGE,"E61"),sQuery(id+"F42.wireOp",EDGE,"E62"),sQuery(id+"F42.wireOp",EDGE,"E63"),sQuery(id+"F42.wireOp",EDGE,"E64"),sQuery(id+"F42.wireOp",EDGE,"E65")])]});
            transform(context, id + "F47", {"entities" : qUnion([Q0]), "transformType" : TransformType.TRANSLATION_3D, "dx" : 0 * mm, "dy" : 625 * mm, "dz" : 0 * mm, "makeCopy" : true});
        }
        {
            var Q0;
            Q0=makeQuery(id+"F43.opExtrude","SWEPT_BODY",BODY,{"disambiguationData":[OSD([sQuery(id+"F42.wireOp",EDGE,"E58"),sQuery(id+"F42.wireOp",EDGE,"E59"),sQuery(id+"F42.wireOp",EDGE,"E60"),sQuery(id+"F42.wireOp",EDGE,"E61"),sQuery(id+"F42.wireOp",EDGE,"E62"),sQuery(id+"F42.wireOp",EDGE,"E63"),sQuery(id+"F42.wireOp",EDGE,"E64"),sQuery(id+"F42.wireOp",EDGE,"E65")])]});
            var Q1;
            Q1=makeQuery(id+"F47.opPattern","COPY",BODY,{"derivedFrom":makeQuery(id+"F43.opExtrude","SWEPT_BODY",BODY,{"disambiguationData":[OSD([sQuery(id+"F42.wireOp",EDGE,"E58"),sQuery(id+"F42.wireOp",EDGE,"E59"),sQuery(id+"F42.wireOp",EDGE,"E60"),sQuery(id+"F42.wireOp",EDGE,"E61"),sQuery(id+"F42.wireOp",EDGE,"E62"),sQuery(id+"F42.wireOp",EDGE,"E63"),sQuery(id+"F42.wireOp",EDGE,"E64"),sQuery(id+"F42.wireOp",EDGE,"E65")])]}),"instanceName":"1"});
            var Q2;
            Q2=qCreatedBy(makeId("Right.planeOp"),FACE);
            mirror(context, id + "F48", {"operationType" : NewBodyOperationType.ADD, "entities" : qUnion([Q0, Q1]), "mirrorPlane" : qUnion([Q2])});
        }
        {
            var Q0;
            Q0=qCreatedBy(makeId("Right.planeOp"),FACE);
            var sketch = newSketch(context, id + "F49", { "sketchPlane" : qUnion([Q0])});
            skLineSegment(sketch, "E67.bottom", {"start": v(-3360, 1844) * mm, "end": v(-6660, 1844) * mm});
            skLineSegment(sketch, "E67.top", {"start": v(-3360, 0) * mm, "end": v(-8020, 0) * mm});
            skLineSegment(sketch, "E67.left", {"start": v(-3360, 1844) * mm, "end": v(-3360, 0) * mm});
            skLineSegment(sketch, "E67.right", {"start": v(-8020, 680) * mm, "end": v(-8020, 0) * mm});
            skLineSegment(sketch, "E68", {"start": v(-8020, 680) * mm, "end": v(-6660, 1844) * mm});
            skSolve(sketch);
        }
        {
            var Q0;
            Q0 = qSketchRegion(id + "F49", true);
            var Q1;
            Q1 = qConstructionFilter(qBodyType(qCreatedBy(id + "F49" ,EDGE), BodyType.WIRE), ConstructionObject.NO);
            extrude(context, id + "F50", {"entities" : qUnion([Q0]), "surfaceEntities" : qUnion([Q1]), "depth" : 940 * mm, "offsetDistance" : 25 * mm, "hasSecondDirection" : true, "secondDirectionOppositeDirection" : true, "secondDirectionDepth" : 940 * mm});
        }
    });
